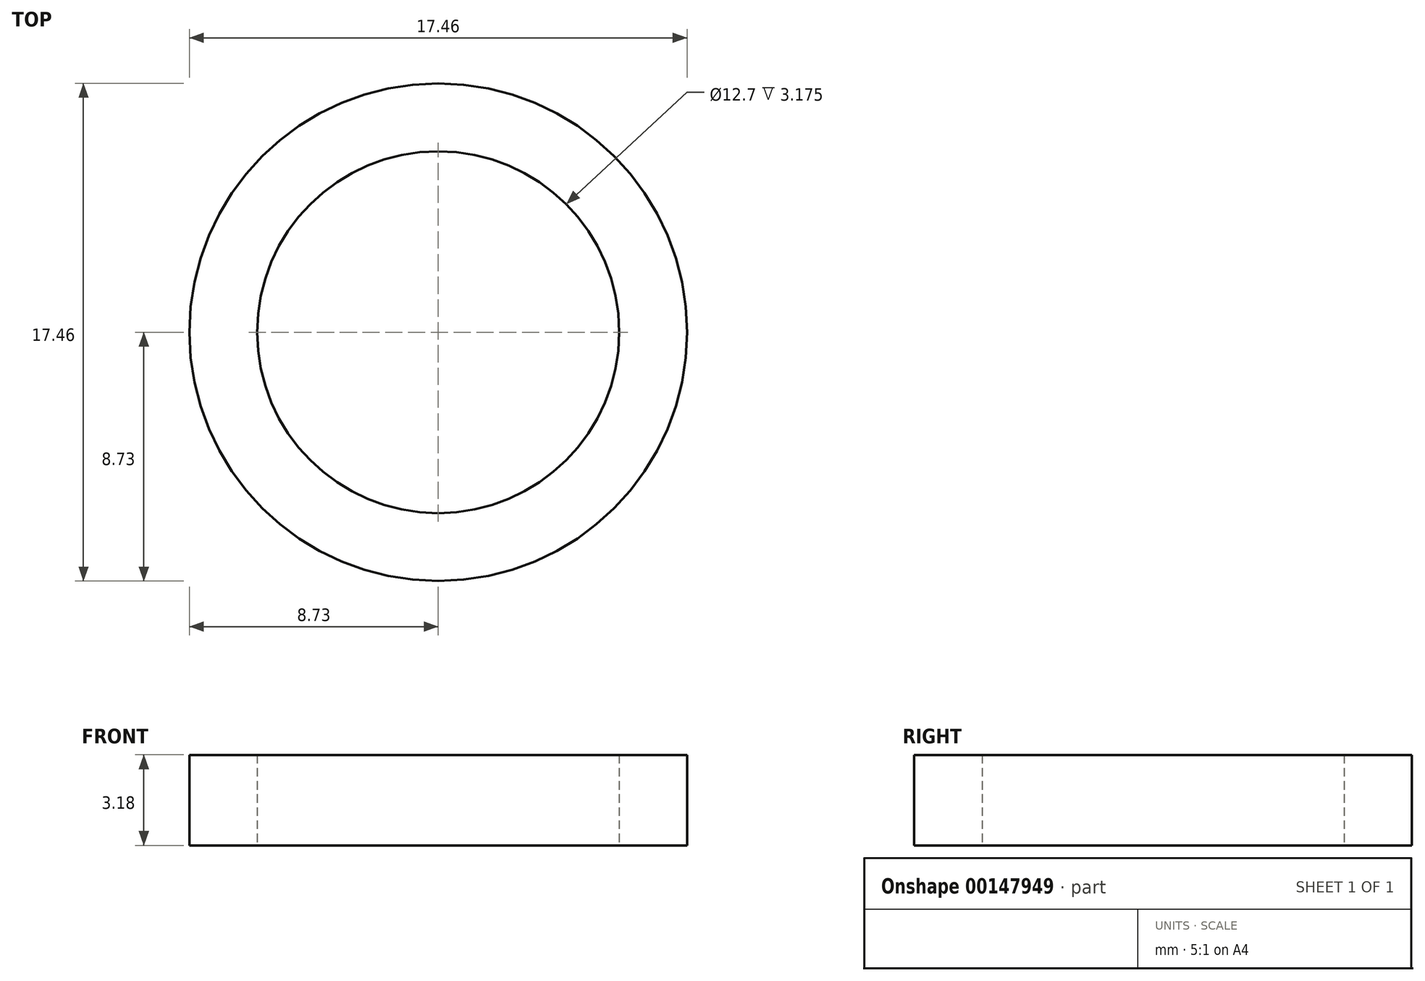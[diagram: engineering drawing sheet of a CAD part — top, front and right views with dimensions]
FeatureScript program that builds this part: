
annotation { "Feature Type Name" : "Feature", "Feature Type Description" : "" }
export const myFeature = defineFeature(function(context is Context, id is Id, definition is map)
    precondition{}
    {
        {
            var Q0;
            Q0=qCreatedBy(makeId("Top.planeOp"),FACE);
            var sketch = newSketch(context, id + "F0", { "sketchPlane" : qUnion([Q0])});
            skCircle(sketch, "E0", {"center": v(0, 0) * mm, "radius": 6.35 * mm});
            skCircle(sketch, "E1", {"center": v(0, 0) * mm, "radius": 8.73 * mm});
            skSolve(sketch);
        }
        {
            var Q0;
            Q0=qSketchRegion(id+"F0",true);
            extrude(context, id + "F1", {"entities" : qUnion([Q0]), "depth" : 3.17 * mm});
        }
    });
